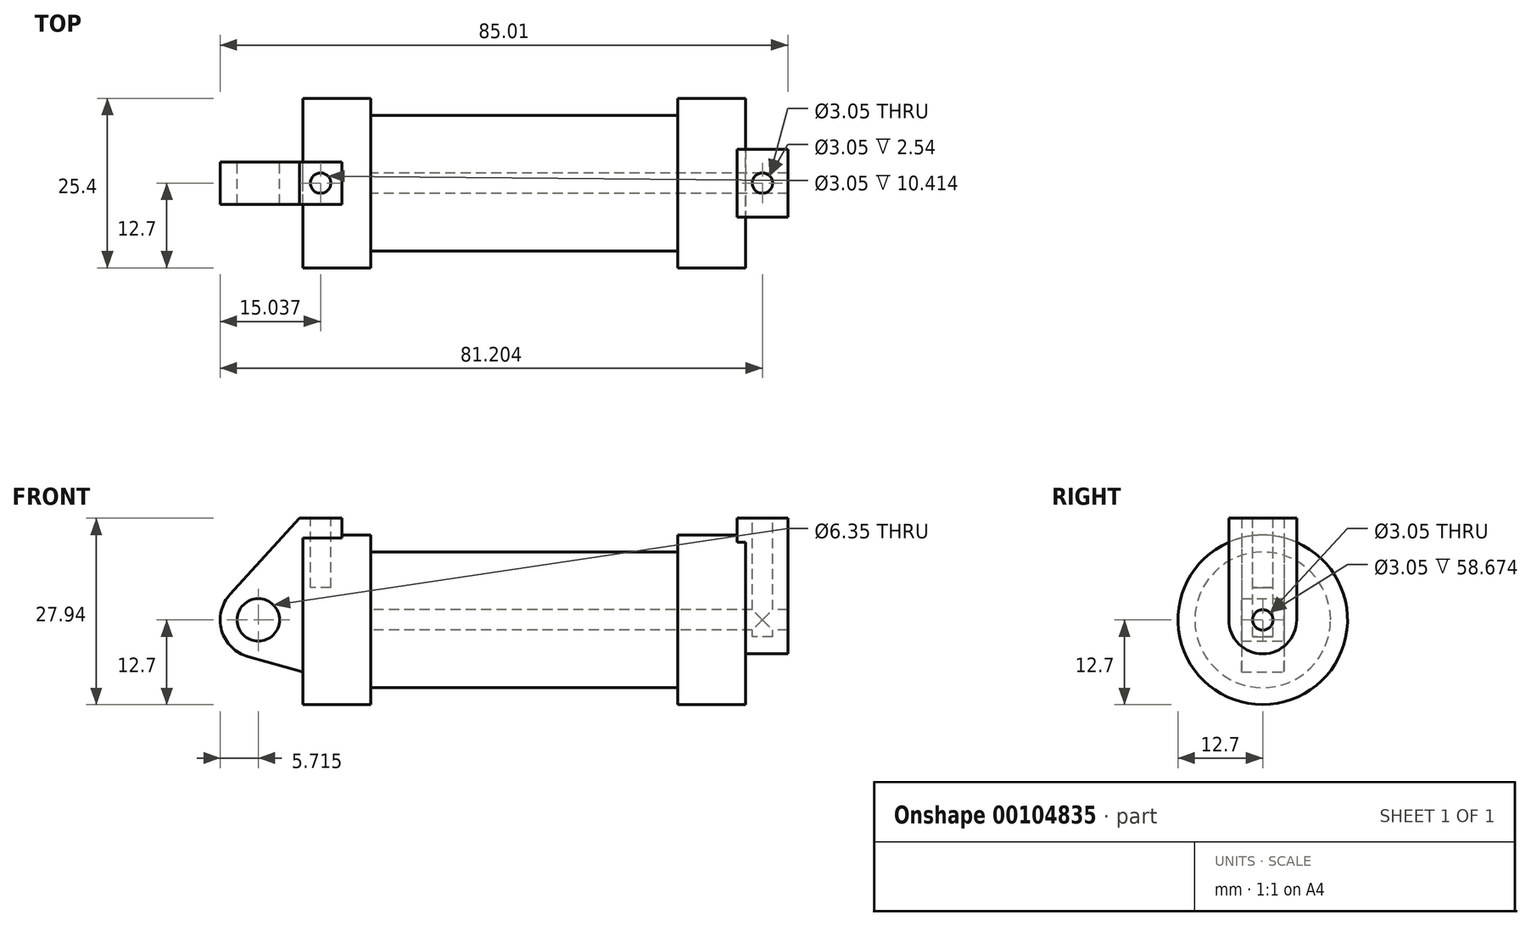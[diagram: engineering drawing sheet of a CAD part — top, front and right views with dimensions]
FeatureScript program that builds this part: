
annotation { "Feature Type Name" : "Feature", "Feature Type Description" : "" }
export const myFeature = defineFeature(function(context is Context, id is Id, definition is map)
    precondition{}
    {
        {
            var Q0;
            Q0=qCreatedBy(makeId("Front.planeOp"),FACE);
            var sketch = newSketch(context, id + "F0", { "sketchPlane" : qUnion([Q0])});
            skLineSegment(sketch, "E0", {"start": v(0, 0) * mm, "end": v(0, 12.7) * mm});
            skLineSegment(sketch, "E1", {"start": v(0, 12.7) * mm, "end": v(10.16, 12.7) * mm});
            skLineSegment(sketch, "E2", {"start": v(10.16, 12.7) * mm, "end": v(10.16, 10.16) * mm});
            skLineSegment(sketch, "E3", {"start": v(10.16, 10.16) * mm, "end": v(56.13, 10.16) * mm});
            skLineSegment(sketch, "E4", {"start": v(56.13, 10.16) * mm, "end": v(56.13, 12.7) * mm});
            skLineSegment(sketch, "E5", {"start": v(56.13, 12.7) * mm, "end": v(66.3, 12.7) * mm});
            skLineSegment(sketch, "E6", {"start": v(66.3, 12.7) * mm, "end": v(66.3, 0) * mm});
            skLineSegment(sketch, "E7", {"start": v(66.3, 0) * mm, "end": v(0, 0) * mm});
            skLineSegment(sketch, "E8", {"start": v(5.84, 15.24) * mm, "end": v(-0.5, 15.24) * mm});
            skLineSegment(sketch, "E9", {"start": v(-0.5, 15.24) * mm, "end": v(-10.88, 3.85) * mm});
            skLineSegment(sketch, "E10", {"start": v(0, 0) * mm, "end": v(-6.65, 0) * mm});
            skCircle(sketch, "E11", {"center": v(-6.65, 0) * mm, "radius": 5.72 * mm});
            skCircle(sketch, "E12", {"center": v(-6.65, 0) * mm, "radius": 3.18 * mm});
            skLineSegment(sketch, "E13", {"start": v(5.84, 15.24) * mm, "end": v(5.84, -9.4) * mm});
            skLineSegment(sketch, "E14", {"start": v(5.84, -9.4) * mm, "end": v(-8.18, -5.5) * mm});
            skSolve(sketch);
        }
        {
            var Q0;
            {var subQ0=sQuery(id+"F0.wireOp",EDGE,"E2");Q0=makeQuery(id+"F0.imprint","IMPRINT",FACE,{"disambiguationData":[TD([[makeQuery(id+"F0.imprint","IMPRINT",EDGE,{"derivedFrom":subQ0}),-1.0]])]});}
            var Q1;
            {var subQ0=sQuery(id+"F0.wireOp",EDGE,"E0");Q1=makeQuery(id+"F0.imprint","IMPRINT",FACE,{"disambiguationData":[TD([[makeQuery(id+"F0.imprint","IMPRINT",EDGE,{"derivedFrom":subQ0}),-1.0]])]});}
            var Q2;
            Q2=sQuery(id+"F0.wireOp",EDGE,"E7");
            revolve(context, id + "F1", {"entities" : qUnion([Q0, Q1]), "axis" : qUnion([Q2]), "revolveType" : RevolveType.FULL});
        }
        {
            var Q0;
            {var subQ0=sQuery(id+"F0.wireOp",EDGE,"E0");Q0=makeQuery(id+"F0.imprint","IMPRINT",FACE,{"disambiguationData":[TD([[makeQuery(id+"F0.imprint","IMPRINT",EDGE,{"derivedFrom":subQ0}),-1.0]])]});}
            var Q1;
            {var subQ3=sQuery(id+"F0.wireOp",EDGE,"E0");Q1=makeQuery(id+"F0.imprint","IMPRINT",FACE,{"disambiguationData":[TD([[makeQuery(id+"F0.imprint","IMPRINT",EDGE,{"derivedFrom":subQ3}),1.0]])]});}
            var Q2;
            {var subQ0=sQuery(id+"F0.wireOp",EDGE,"E14");Q2=makeQuery(id+"F0.imprint","IMPRINT",FACE,{"disambiguationData":[TD([[makeQuery(id+"F0.imprint","IMPRINT",EDGE,{"derivedFrom":subQ0}),-1.0]])]});}
            var Q3;
            {var subQ4=sQuery(id+"F0.wireOp",EDGE,"E12");Q3=makeQuery(id+"F0.imprint","IMPRINT",FACE,{"disambiguationData":[TD([[makeQuery(id+"F0.imprint","IMPRINT",EDGE,{"derivedFrom":subQ4}),-1.0]])]});}
            extrude(context, id + "F2", {"entities" : qUnion([Q0, Q1, Q2, Q3]), "operationType" : NewBodyOperationType.ADD, "endBound" : BoundingType.SYMMETRIC, "depth" : 6.35 * mm});
        }
        {
            var Q0;
            Q0=makeQuery(id+"F1.opRevolve","SWEPT_FACE",FACE,{"disambiguationData":[OSD([sQuery(id+"F0.wireOp",EDGE,"E6")])]});
            var sketch = newSketch(context, id + "F3", { "sketchPlane" : qUnion([Q0])});
            skCircle(sketch, "E15", {"center": v(0, 0) * mm, "radius": 1.52 * mm});
            skCircle(sketch, "E16", {"center": v(0, 0) * mm, "radius": 5.08 * mm});
            skLineSegment(sketch, "E17", {"start": v(-5.08, 0) * mm, "end": v(-5.08, 15.24) * mm});
            skLineSegment(sketch, "E18", {"start": v(5.08, 0) * mm, "end": v(5.08, 15.24) * mm});
            skLineSegment(sketch, "E19", {"start": v(-5.08, 15.24) * mm, "end": v(5.08, 15.24) * mm});
            skSolve(sketch);
        }
        {
            var Q0;
            Q0 = qSketchRegion(id + "F3", true);
            extrude(context, id + "F4", {"entities" : qUnion([Q0]), "operationType" : NewBodyOperationType.ADD, "depth" : 6.35 * mm, "hasSecondDirection" : true, "secondDirectionOppositeDirection" : true, "secondDirectionDepth" : 1.27 * mm});
        }
        {
            var Q0;
            Q0=makeQuery(id+"F4.opExtrude","SWEPT_FACE",FACE,{"disambiguationData":[OSD([sQuery(id+"F3.wireOp",EDGE,"E19")])]});
            var sketch = newSketch(context, id + "F5", { "sketchPlane" : qUnion([Q0])});
            skCircle(sketch, "E20", {"center": v(68.83, 0) * mm, "radius": 1.52 * mm});
            skPoint(sketch, "E20.centerSnap0", {"position": v(68.83, 5.08) * mm});
            skPoint(sketch, "E20.centerSnap1", {"position": v(72.64, 0) * mm});
            skSolve(sketch);
        }
        {
            var Q0;
            Q0=makeQuery(id+"F2.opExtrude","SWEPT_FACE",FACE,{"disambiguationData":[OSD([sQuery(id+"F0.wireOp",EDGE,"E8")])]});
            var sketch = newSketch(context, id + "F6", { "sketchPlane" : qUnion([Q0])});
            skCircle(sketch, "E21", {"center": v(2.67, 0) * mm, "radius": 1.52 * mm});
            skPoint(sketch, "E21.centerSnap0", {"position": v(2.67, 3.18) * mm});
            skPoint(sketch, "E21.centerSnap1", {"position": v(-0.5, 0) * mm});
            skSolve(sketch);
        }
        {
            var Q0;
            Q0=makeQuery(id+"F5.imprint","IMPRINT",FACE,{"disambiguationData":[TD([[makeQuery(id+"F5.imprint","IMPRINT",EDGE,{"derivedFrom":sQuery(id+"F5.wireOp",EDGE,"E20")}),1.0]])]});
            extrude(context, id + "F7", {"entities" : qUnion([Q0]), "operationType" : NewBodyOperationType.REMOVE, "oppositeDirection" : true, "depth" : 17.78 * mm});
        }
        {
            var Q0;
            Q0=makeQuery(id+"F6.imprint","IMPRINT",FACE,{"disambiguationData":[TD([[makeQuery(id+"F6.imprint","IMPRINT",EDGE,{"derivedFrom":sQuery(id+"F6.wireOp",EDGE,"E21")}),1.0]])]});
            extrude(context, id + "F8", {"entities" : qUnion([Q0]), "operationType" : NewBodyOperationType.REMOVE, "oppositeDirection" : true, "depth" : 10.4 * mm});
        }
        {
            var Q0;
            Q0=makeQuery(id+"F4.boolean.opBoolean","SPLIT",FACE,{"disambiguationData":[TD([makeQuery(id+"F4.opExtrude","SWEPT_FACE",FACE,{"disambiguationData":[OSD([sQuery(id+"F3.wireOp",EDGE,"E15")])]})])],"derivedFrom":makeQuery(id+"F1.opRevolve","SWEPT_FACE",FACE,{"disambiguationData":[OSD([sQuery(id+"F0.wireOp",EDGE,"E6")])]})});
            var Q1;
            Q1=makeQuery(id+"F1.opRevolve","SWEPT_FACE",FACE,{"disambiguationData":[OSD([sQuery(id+"F0.wireOp",EDGE,"E2")])]});
            extrude(context, id + "F9", {"entities" : qUnion([Q0]), "operationType" : NewBodyOperationType.REMOVE, "endBound" : BoundingType.UP_TO_SURFACE, "oppositeDirection" : true, "endBoundEntityFace" : qUnion([Q1]), "depth" : 25.4 * mm});
        }
    });
